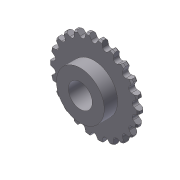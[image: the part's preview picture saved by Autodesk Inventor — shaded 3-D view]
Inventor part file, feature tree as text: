
AUTODESK INVENTOR PART (.ipt)
format: ipt  version: 2012 (Build 160160000, 160)  size: 248,832 bytes
history: native  units: in
note: dims shown in document units (in); Inventor stores cm internally (conversion verified against a paired STEP export)
features: extrude x3, sketch x3, chamfer x1, pattern_circular x1
ambient origin geometry x8: Origin, YZ Plane, XZ Plane, XY Plane, X Axis, Y Axis, Z Axis, Center Point
bodies: Solid1 (feature_tree)
feature tree (8):
  extrude  "Extrusion1"  Depth=0.5in
  extrude  "Extrusion2"  Depth=1.0in
  extrude  "Extrusion3"  Depth=0.0625in
  chamfer  "Chamfer1"  Distance=0.0625in
  pattern_circular  "Circular Pattern1"  Angle=60.0deg  [1 undecoded]
  sketch  "Sketch1"  dims[d0=1.87in d1=0.5in]
  sketch  "Sketch2"  dims[d2=0.123in d3=0.0in d4=1.0in]
  sketch  "Sketch3"  dims[d5=0.282in d6=0.0in d7=0.0625in d8=0.0625in d9=60.0deg d10=0.28in d11=0.0in d12=0.0312in d13=0.125in d14=45.0deg d15=8.6614in d16=360.0deg]
note: 1 required parameter value undecoded (feature->parameter linkage not recoverable at this tier; creation-order binding heuristic only, values carry confidence <= 0.55)
